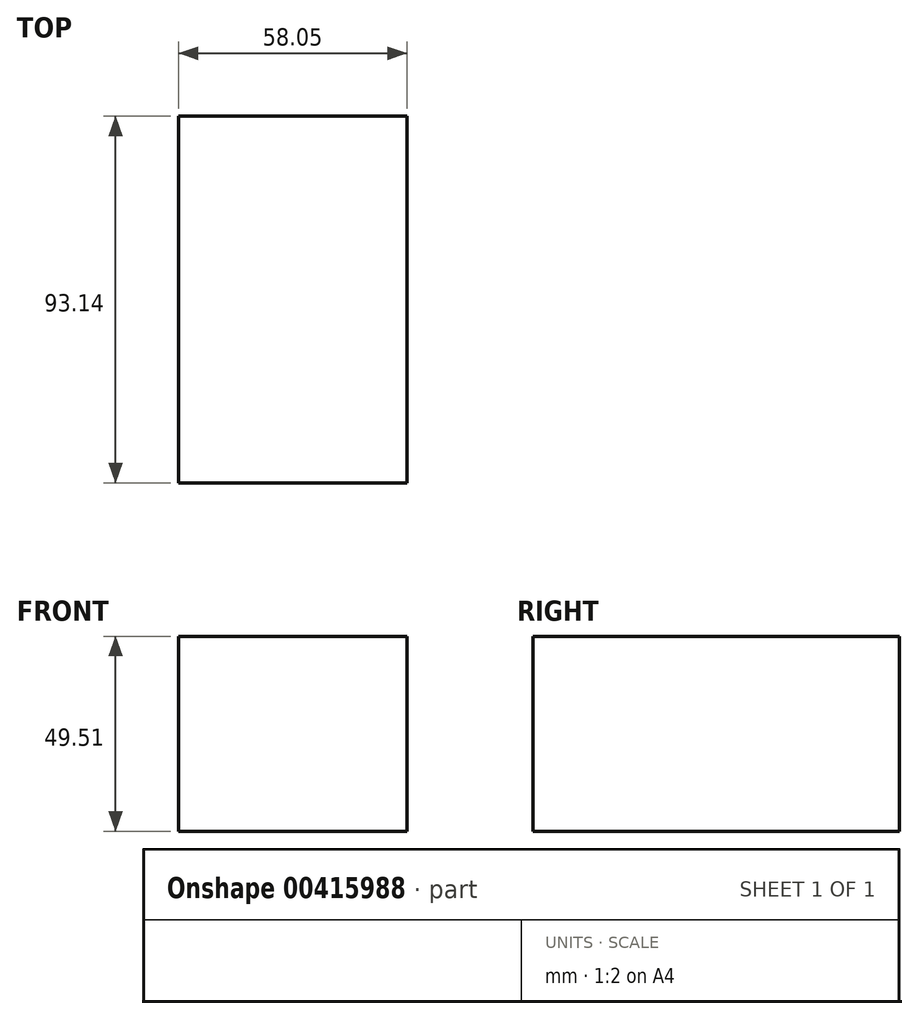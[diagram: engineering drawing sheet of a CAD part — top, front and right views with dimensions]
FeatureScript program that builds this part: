
annotation { "Feature Type Name" : "Feature", "Feature Type Description" : "" }
export const myFeature = defineFeature(function(context is Context, id is Id, definition is map)
    precondition{}
    {
        {
            var Q0;
            Q0=qCreatedBy(makeId("Front.planeOp"),FACE);
            var sketch = newSketch(context, id + "F0", { "sketchPlane" : qUnion([Q0])});
            skLineSegment(sketch, "E0.bottom", {"start": v(0, 12.27) * mm, "end": v(58.05, 12.27) * mm});
            skLineSegment(sketch, "E0.top", {"start": v(0, 61.78) * mm, "end": v(58.05, 61.78) * mm});
            skLineSegment(sketch, "E0.left", {"start": v(0, 12.27) * mm, "end": v(0, 61.78) * mm});
            skLineSegment(sketch, "E0.right", {"start": v(58.05, 12.27) * mm, "end": v(58.05, 61.78) * mm});
            skSolve(sketch);
        }
        {
            var Q0;
            Q0=makeQuery(id+"F0.imprint","IMPRINT",FACE,{"disambiguationData":[TD([[makeQuery(id+"F0.imprint","IMPRINT",EDGE,{"derivedFrom":sQuery(id+"F0.wireOp",EDGE,"E0.bottom")}),1.0]])]});
            extrude(context, id + "F1", {"entities" : qUnion([Q0]), "depth" : 93.14 * mm});
        }
    });
